# Revit family: light_sensor_dual_058326
name_source: partatom
category: Elektroinstallationen
revit_build: Autodesk Revit 2016 (Build: 20190508_0715(x64)
units: mm (PartAtom-declared; Revit-internal decimal feet)

## family parameters
Basisbauteil = Fläche
Beim Laden mit Abzugskörper schneiden = Nein
Bemaßung runder Anschluss = Durchmesser verwenden
Beschriftungsausrichtung beibehalten = Nein
Gemeinsam genutzt = Nein
Raumberechnungspunkt = Nein
Teiletyp = Normal

## types (1)
- Light Sensor Dual
    Apparent Load = 0 VA
    Beschreibung = Type: Constant-lighting controller; Dimensions (L x W x H): 51 x 94 x 94 mm; Sensor Technology: Light sensor; Application, place: Indoors; Application, room: classroom, one-person office, open-plan office, high-bay warehouse, conference room / meeting room, Indoors; Installation site: wall, ceiling; Installation: Concealed wiring; Mounting height: 2,00 – 4,00 m; Twilight setting: 2 – 1000 lx; Basic light level function: Yes; KNX functions: Light output 2x, Light level, Constant-lighting control, Photo-cell controller; With bus coupling: Yes; Settings via: ETS software, Remote control, Bus, Smart Remote; IP-rating: IP20; Version: KNX - concealed, sq.; PU1, EAN: 4007841058326
    Height = 94 mm  [stored 0.308399 ft]
    Hersteller = Steinel
    Length = 51 mm
    ModVariant = Nein
    Modell = 058326
    Mounting Type = Recessed
    Number of Poles = 1
    OnlyDefault = Ja
    Power Factor = 1
    Product Name = Light Sensor Dual
    Product group = Sensor-switched indoor light
    ProductGroupID = 30
    Protection Class = Protection class
    Protection Degree = IP 20
    RlxData = <blob elided: 23893 chars, md5=083edc99>
    SensorDataFile = {"IESDataFiles":[]}
    Typenbild = produkt1_058326.jpg
    Typenkommentare = Product without accessories
    URL = http://relux.com
    VarID = ---
    Voltage = 0 V
    Vorgabe-Ansicht = 1800 mm
    Weight = 0.00 kg
    Width = 94 mm  [stored 0.308399 ft]

note: [stored X ft] marks values corroborated as IEEE doubles in the binary element streams (Revit-internal decimal feet)

## geometry (parser evidence)
native form markers: Blend x4, Sweep x14
no freeform markers — native parametric forms only
